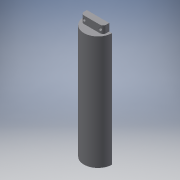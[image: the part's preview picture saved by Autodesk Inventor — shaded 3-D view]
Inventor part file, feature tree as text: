
AUTODESK INVENTOR PART (.ipt)
format: ipt  version: 2019 (Build 230136000, 136)  size: 247,296 bytes
history: native  units: in
note: dims shown in document units (in); Inventor stores cm internally (conversion verified against a paired STEP export)
features: reference x18, sketch x12, extrude x11, projected_geometry x4, other x3, plane x1, fillet x1
ambient origin geometry x8: Origin, YZ Plane, XZ Plane, XY Plane, X Axis, Y Axis, Z Axis, Center Point
bodies: Solid1 (feature_tree)
feature tree (50):
  extrude  "Extrusion1"  Depth=1.1417in
  extrude  "Extrusion2"  Depth=2.0in TaperAngle=0.0deg
  sketch  "Sketch4"  dims[d9=0.125in d10=0.0in d13=0.25in]
  extrude  "Extrusion4"  Depth=0.125in
  extrude  "Extrusion5"  Depth=0.25in
  extrude  "Extrusion6"  Depth=0.3in TaperAngle=0.0deg
  extrude  "Extrusion7"  Depth=0.25in
  extrude  "Extrusion8"  Depth=0.3in TaperAngle=0.0deg
  extrude  "Extrusion9"  Depth=0.25in TaperAngle=0.0deg
  sketch  "Sketch11"  dims[d32=0.25in d33=0.0in d34=0.3in d35=0.0in]
  plane  "Work Plane1"
  extrude  "Extrusion10"  Depth=0.125in
  extrude  "Extrusion11"  Depth=0.3in TaperAngle=0.0deg
  extrude  "Extrusion12"  Depth=0.125in
  fillet  "Fillet1"  [1 undecoded]
  sketch  "Sketch1"  dims[d2=0.675in d3=1.1417in]
  reference  "Reference1"
  reference  "Reference2"
  reference  "Reference3"
  reference  "Reference4"
  sketch  "Sketch2"  dims[d4=1.042in d5=2.0in d6=2.5in d7=0.0in d8=0.0in]
  sketch  "Sketch5"  dims[d14=0.25in d15=0.25in]
  reference  "Reference11"
  reference  "Reference12"
  sketch  "Sketch6"  dims[d16=0.3in d17=0.0in d18=0.3in d19=0.0in]
  projected_geometry  "Projected Loop1"
  projected_geometry  "Projected Loop2"
  sketch  "Sketch7"  dims[d20=0.2in d21=0.0in d22=0.25in]
  reference  "Reference13"
  reference  "Reference14"
  sketch  "Sketch8"  dims[d23=0.25in d24=0.3in d25=0.0in]
  reference  "Reference15"
  sketch  "Sketch9"  dims[d26=0.2in d27=0.0in d28=0.25in d29=0.0in]
  reference  "Reference16"
  reference  "Reference17"
  sketch  "Sketch10"  dims[d30=0.25in d31=0.125in]
  projected_geometry  "Projected Loop3"
  projected_geometry  "Projected Loop4"
  reference  "Reference18"
  sketch  "Sketch12"  dims[d36=1.0in d37=0.0in d38=0.125in]
  reference  "Reference19"
  reference  "Reference20"
  reference  "Reference21"
  reference  "Reference22"
  sketch  "Sketch13"
  reference  "Reference23"
  reference  "Reference24"
  other  "Rocket Case.iam"
  other  "Rocket_Data_Logger v1:1"
  other  "Tube Top:1"
note: 1 required parameter value undecoded (feature->parameter linkage not recoverable at this tier; creation-order binding heuristic only, values carry confidence <= 0.55)
